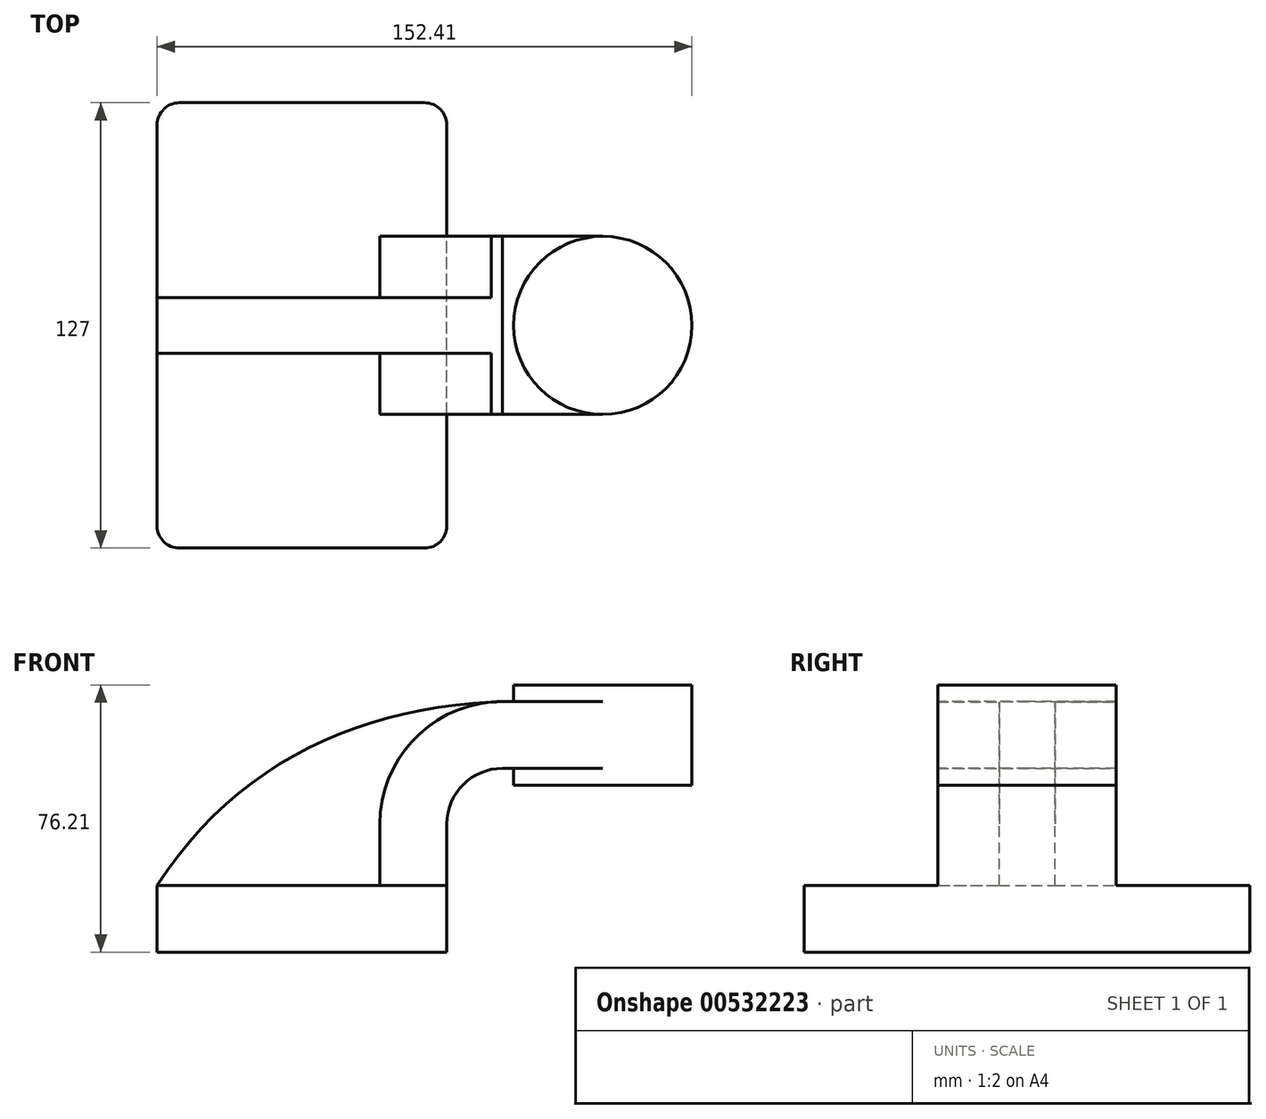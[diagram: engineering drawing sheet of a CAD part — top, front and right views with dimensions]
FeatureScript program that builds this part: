
annotation { "Feature Type Name" : "Feature", "Feature Type Description" : "" }
export const myFeature = defineFeature(function(context is Context, id is Id, definition is map)
    precondition{}
    {
        {
            var Q0;
            Q0=qCreatedBy(makeId("Front.planeOp"),FACE);
            var sketch = newSketch(context, id + "F0", { "sketchPlane" : qUnion([Q0])});
            skLineSegment(sketch, "E0.bottom", {"start": v(-41.28, -9.53) * mm, "end": v(41.28, -9.53) * mm});
            skLineSegment(sketch, "E0.top", {"start": v(-41.28, 9.52) * mm, "end": v(41.28, 9.52) * mm});
            skLineSegment(sketch, "E0.left", {"start": v(-41.28, -9.53) * mm, "end": v(-41.28, 9.53) * mm});
            skLineSegment(sketch, "E0.right", {"start": v(41.28, -9.53) * mm, "end": v(41.28, 9.52) * mm});
            skPoint(sketch, "E0.middle", {"position": v(0, 0) * mm});
            skLineSegment(sketch, "E1.bottom", {"start": v(60.33, 38.1) * mm, "end": v(111.13, 38.1) * mm});
            skLineSegment(sketch, "E1.top", {"start": v(60.33, 66.67) * mm, "end": v(111.13, 66.67) * mm});
            skLineSegment(sketch, "E1.left", {"start": v(60.33, 38.1) * mm, "end": v(60.33, 66.67) * mm});
            skLineSegment(sketch, "E1.right", {"start": v(111.13, 38.1) * mm, "end": v(111.13, 66.68) * mm});
            skPoint(sketch, "E1.middle", {"position": v(85.73, 52.39) * mm});
            skLineSegment(sketch, "E2", {"start": v(41.27, 9.52) * mm, "end": v(41.27, 27) * mm});
            skArc(sketch, "E3", {"start": v(41.27, 27) * mm, "mid": v(45.92, 38.23) * mm, "end": v(57.15, 42.88) * mm});
            skLineSegment(sketch, "E4", {"start": v(57.15, 42.88) * mm, "end": v(85.72, 42.88) * mm});
            skLineSegment(sketch, "E5.0", {"start": v(57.15, 61.93) * mm, "end": v(85.72, 61.93) * mm});
            skArc(sketch, "E5.1", {"start": v(22.23, 27) * mm, "mid": v(32.45, 51.7) * mm, "end": v(57.15, 61.93) * mm});
            skLineSegment(sketch, "E5.2", {"start": v(22.22, 9.52) * mm, "end": v(22.22, 27) * mm});
            skLineSegment(sketch, "E6", {"start": v(85.73, 38.1) * mm, "end": v(85.73, 66.67) * mm});
            skFitSpline(sketch, "E7", {"points": [v(-41.28, 9.53) * mm, v(57.15, 61.93) * mm], "startDerivative": vector(68.42, 105.04) * mm, "endDerivative": vector(123.02, 4.47) * mm});
            skSolve(sketch);
        }
        {
            var Q0;
            Q0=makeQuery(id+"F0.imprint","IMPRINT",FACE,{"disambiguationData":[TD([[makeQuery(id+"F0.imprint","IMPRINT",EDGE,{"derivedFrom":sQuery(id+"F0.wireOp",EDGE,"E0.bottom")}),1.0]])]});
            extrude(context, id + "F1", {"entities" : qUnion([Q0]), "endBound" : BoundingType.SYMMETRIC, "depth" : 127 * mm, "offsetDistance" : 25.4 * mm});
        }
        {
            var Q0;
            {var subQ1=sQuery(id+"F0.wireOp",EDGE,"E2");Q0=makeQuery(id+"F0.imprint","IMPRINT",FACE,{"disambiguationData":[TD([[makeQuery(id+"F0.imprint","IMPRINT",EDGE,{"derivedFrom":subQ1}),1.0]])]});}
            extrude(context, id + "F2", {"entities" : qUnion([Q0]), "operationType" : NewBodyOperationType.ADD, "endBound" : BoundingType.SYMMETRIC, "depth" : 50.8 * mm, "offsetDistance" : 25.4 * mm});
        }
        {
            var Q0;
            {var subQ3=sQuery(id+"F0.wireOp",EDGE,"E5.2");Q0=makeQuery(id+"F0.imprint","IMPRINT",FACE,{"disambiguationData":[TD([[makeQuery(id+"F0.imprint","IMPRINT",EDGE,{"derivedFrom":subQ3}),1.0]])]});}
            extrude(context, id + "F3", {"entities" : qUnion([Q0]), "operationType" : NewBodyOperationType.ADD, "endBound" : BoundingType.SYMMETRIC, "depth" : 15.88 * mm, "offsetDistance" : 25.4 * mm});
        }
        {
            var Q0;
            {var subQ0=sQuery(id+"F0.wireOp",EDGE,"E4");var subQ1=sQuery(id+"F0.wireOp",EDGE,"E1.left");var subQ2=makeQuery(id+"F0.imprint","INTERSECT",VERTEX,{"derivedFrom":[subQ1,subQ0]});Q0=makeQuery(id+"F0.imprint","IMPRINT",FACE,{"disambiguationData":[TD([[makeQuery(id+"F0.imprint","IMPRINT",EDGE,{"disambiguationData":[TD([[subQ2,-1.0]])],"derivedFrom":subQ1}),-1.0]])]});}
            extrude(context, id + "F4", {"entities" : qUnion([Q0]), "operationType" : NewBodyOperationType.ADD, "endBound" : BoundingType.SYMMETRIC, "depth" : 50.8 * mm, "offsetDistance" : 25.4 * mm});
        }
        {
            var Q0;
            {var subQ4=sQuery(id+"F0.wireOp",EDGE,"E1.right");Q0=makeQuery(id+"F0.imprint","IMPRINT",FACE,{"disambiguationData":[TD([[makeQuery(id+"F0.imprint","IMPRINT",EDGE,{"derivedFrom":subQ4}),1.0]])]});}
            var Q1;
            Q1=sQuery(id+"F0.wireOp",EDGE,"E6");
            revolve(context, id + "F5", {"operationType" : NewBodyOperationType.ADD, "entities" : qUnion([Q0]), "axis" : qUnion([Q1]), "revolveType" : RevolveType.FULL});
        }
        {
            var Q0;
            Q0=makeQuery(id+"F1.opExtrude","CAP_EDGE",EDGE,{"disambiguationData":[OSD([sQuery(id+"F0.wireOp",EDGE,"E0.left")])],"isStart":false});
            var Q1;
            Q1=makeQuery(id+"F1.opExtrude","CAP_EDGE",EDGE,{"disambiguationData":[OSD([sQuery(id+"F0.wireOp",EDGE,"E0.right")])],"isStart":false});
            var Q2;
            Q2=makeQuery(id+"F1.opExtrude","CAP_EDGE",EDGE,{"disambiguationData":[OSD([sQuery(id+"F0.wireOp",EDGE,"E0.right")])],"isStart":true});
            fillet(context, id + "F6", {"entities" : qUnion([Q0, Q1, Q2]), "radius" : 6.35 * mm, "tangentPropagation" : true, "allowEdgeOverflow" : false});
        }
        {
            var Q0;
            Q0=makeQuery(id+"F1.opExtrude","CAP_EDGE",EDGE,{"disambiguationData":[OSD([sQuery(id+"F0.wireOp",EDGE,"E0.left")])],"isStart":true});
            fillet(context, id + "F7", {"entities" : qUnion([Q0]), "radius" : 6.35 * mm, "tangentPropagation" : true, "allowEdgeOverflow" : false});
        }
    });
